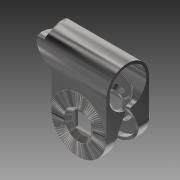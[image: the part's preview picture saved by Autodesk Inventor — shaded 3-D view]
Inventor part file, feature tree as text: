
AUTODESK INVENTOR PART (.ipt)
format: ipt  version: 2021 (Build 250183000, 183)  size: 1,640,448 bytes
history: native  units: mm
features: sketch x13, extrude x12, other x7, fillet x3, revolve x1, pattern_circular x1, mirror x1
ambient origin geometry x8: Origin, YZ Plane, XZ Plane, XY Plane, X Axis, Y Axis, Z Axis, Center Point
bodies: Body1 (feature_tree)
feature tree (38):
  other  "Sólido1"
  revolve  "Revolución1"  [1 undecoded]
  extrude  "Extrusión1"  Depth=7.5mm
  extrude  "Extrusión2"  Depth=1.5mm
  other  "Suprimir cara1"
  sketch  "Boceto4"  dims[d8=9.5mm d9=5.0mm]
  sketch  "Boceto5"  dims[d13=5.0mm d15=1.5mm]
  extrude  "Extrusión3"  Depth=5.0mm
  other  "Suprimir cara2"
  other  "Suprimir cara3"
  other  "Suprimir cara4"
  extrude  "Extrusión4"  Depth=1.5mm
  other  "Suprimir cara5"
  extrude  "Extrusión5"  TaperAngle=90.0deg  [1 undecoded]
  other  "Suprimir cara6"
  sketch  "Boceto8"  dims[d22=10.0mm d23=0.0mm d31=21.0mm d32=25.0mm]
  extrude  "Extrusión7"  Depth=9.0mm
  extrude  "Extrusión8"  Depth=10.0mm
  fillet  "Empalme4"  Radius=25.0mm
  extrude  "Extrusión9"  Depth=16.0mm TaperAngle=0.0deg
  pattern_circular  "Patrón circular2"  Count=4  [1 undecoded]
  mirror  "Simetría1"
  extrude  "Extrusión10"  Depth=12.5mm
  extrude  "Extrusión11"  Depth=2.0mm
  extrude  "Extrusión12"  Depth=2.0mm TaperAngle=0.0deg
  extrude  "Extrusión13"  Depth=2.0mm
  fillet  "Empalme5"  Radius=2.5mm
  fillet  "Empalme6"  Radius=0.5mm
  sketch  "Boceto1"  dims[d0=11.0mm d1=1.5mm]
  sketch  "Boceto2"  dims[d4=8.5mm d5=7.5mm]
  sketch  "Boceto3"  dims[d6=11.0mm d7=1.5mm]
  sketch  "Boceto6"  dims[d16=1.5mm d17=90.0deg]
  sketch  "Boceto7"  dims[d20=9.0mm d21=9.0mm]
  sketch  "Boceto9"  dims[d33=22.0mm d34=16.0mm d35=16.0mm d36=0.0mm d37=0.0mm]
  sketch  "Boceto10"  dims[d38=1.5mm d39=40.0mm]
  sketch  "Boceto11"  dims[d40=12.5mm d41=20.5mm]
  sketch  "Boceto12"  dims[d42=20.5mm d43=2.0mm]
  sketch  "Boceto13"  dims[d44=32.0mm d45=0.0mm d46=2.5mm d47=0.0mm d48=20.5mm d49=2.5mm d50=0.0mm d51=0.5mm d52=0.25mm d53=0.25mm d59=2.5mm d60=2.5mm d61=0.0mm d62=0.5mm d63=0.0mm d65=0.5mm d66=0.5mm d67=0.0mm d68=470.0mm d69=360.0deg d71=8.0mm d72=0.0mm d73=1.5mm d74=4.0mm d75=0.0mm d76=1.5mm d77=7.0mm d78=3.5mm d79=0.0mm d80=0.0mm d81=1.5mm d82=7.0mm d83=3.5mm d84=0.0mm d85=0.0mm d86=2.0mm d87=2.0mm]
note: 3 required parameter values undecoded (feature->parameter linkage not recoverable at this tier; creation-order binding heuristic only, values carry confidence <= 0.55)